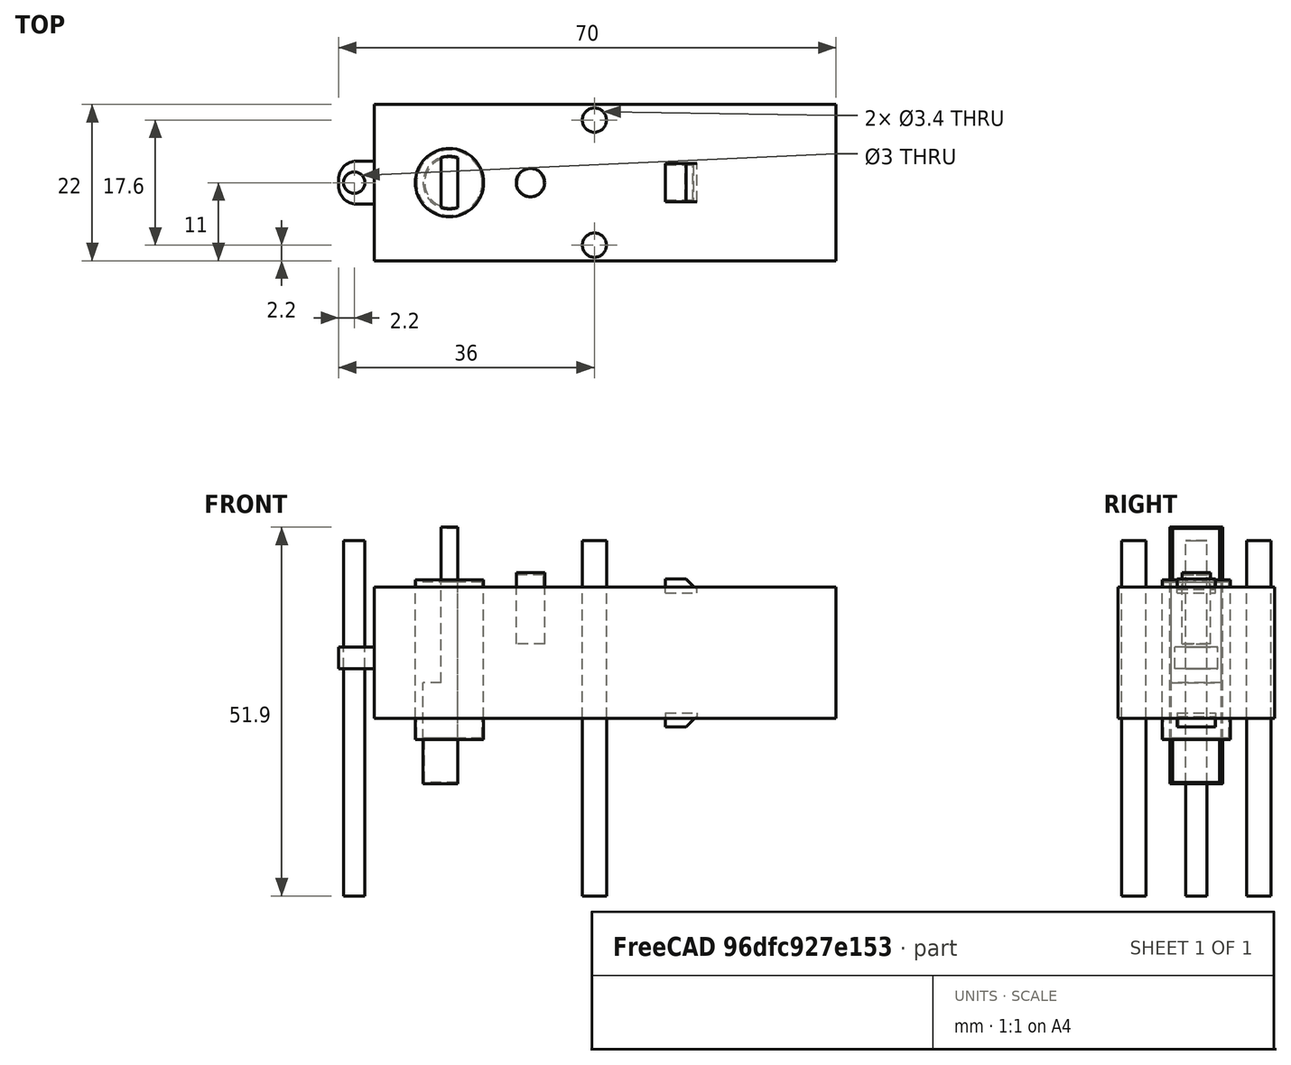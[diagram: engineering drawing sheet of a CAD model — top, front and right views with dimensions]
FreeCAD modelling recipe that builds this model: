
FCSTD DOCUMENT  (FreeCAD 0.16R6703 (Git))
Label: winder
License: All rights reserved
LicenseURL: http://en.wikipedia.org/wiki/All_rights_reserved
objects: Part::Cylinder×12, Part::Box×10, Part::Cut×7, Part::Fuse×7, Part::Chamfer×4, Part::Fillet×2, Part::Mirroring×2, App::DocumentObjectGroup×1
note: 44 computed .brp shape members not serialized (recipe doc carries the construction recipe); baked Part::Feature solids carry a one-line shape summary decoded from their .brp

FEATURE [Part::Box] Box  label="Cube"
  Height = 18.5
  Length = 65
  Placement = pos=(0,-11,0) rot=(0,0,1;0rad)
  Width = 22
FEATURE [Part::Box] Box001  label="Cube001"
  Height = 3
  Length = 10
  Placement = pos=(-5,-3,7) rot=(0,0,1;0rad)
  Width = 6
FEATURE [Part::Cylinder] Cylinder
  Angle = 360
  Height = 10
  Placement = pos=(-2.8,0,3) rot=(0,0,1;0rad)
  Radius = 1.5
FEATURE [Part::Cut] Cut
  Base = -> Box001
  Tool = -> Cylinder
FEATURE [Part::Fillet] Fillet
  Base = -> Cut
  Edges = 1 edges r=2.5: [Edge1]
FEATURE [Part::Fillet] Fillet001
  Base = -> Fillet
  Edges = 1 edges r=2.5: [Edge3]
FEATURE [Part::Cylinder] Cylinder001  label="endhole"
  Angle = 360
  Height = 50
  Placement = pos=(-2.8,0,-25) rot=(0,0,1;0rad)
  Radius = 1.5
FEATURE [Part::Fuse] Fusion
  Base = -> Box
  Tool = -> Fillet001
FEATURE [Part::Cylinder] Cylinder002  label="Cylinder001"
  Angle = 360
  Height = 50
  Placement = pos=(31,8.8,-25) rot=(0,0,1;0rad)
  Radius = 1.7
FEATURE [Part::Cylinder] Cylinder003  label="Cylinder002"
  Angle = 360
  Height = 50
  Placement = pos=(31,-8.8,-25) rot=(0,0,1;0rad)
  Radius = 1.7
FEATURE [Part::Cylinder] Cylinder004  label="body-hole-1"
  Angle = 360
  Height = 50
  Placement = pos=(31,8.8,-25) rot=(0,0,1;0rad)
  Radius = 1.7
FEATURE [Part::Cylinder] Cylinder005  label="body-hole-2"
  Angle = 360
  Height = 50
  Placement = pos=(31,-8.8,-25) rot=(0,0,1;0rad)
  Radius = 1.7
FEATURE [Part::Cut] Cut001
  Base = -> Fusion
  Tool = -> Cylinder002
FEATURE [Part::Cut] Cut002
  Base = -> Cut001
  Tool = -> Cylinder003
FEATURE [Part::Cylinder] Cylinder006  label="Cylinder003"
  Angle = 360
  Height = 10
  Placement = pos=(22,0,10.2) rot=(0,0,1;0rad)
  Radius = 1.85
FEATURE [Part::Cylinder] Cylinder007  label="central-bump"
  Angle = 360
  Height = 10
  Placement = pos=(22,0,10.5) rot=(0,0,1;0rad)
  Radius = 2
FEATURE [Part::Fuse] Fusion001
  Base = -> Cut002
  Tool = -> Cylinder006
FEATURE [Part::Cylinder] Cylinder008  label="Cylinder004"
  Angle = 360
  Height = 22
  Placement = pos=(10.6,0,-2.8) rot=(0,0,1;0rad)
  Radius = 4.6
FEATURE [Part::Cylinder] Cylinder009  label="motor-boss"
  Angle = 360
  Height = 22.5
  Placement = pos=(10.6,0,-3) rot=(0,0,1;0rad)
  Radius = 4.8
FEATURE [Part::Fuse] Fusion002
  Base = -> Fusion001
  Tool = -> Cylinder008
FEATURE [Part::Cylinder] Cylinder010  label="motor-boss001"
  Angle = 360
  Height = 35.7
  Placement = pos=(10.6,0,-9) rot=(0,0,1;0rad)
  Radius = 3.5
FEATURE [Part::Box] Box002  label="Cube002"
  Height = 40
  Length = 10
  Placement = pos=(11.75,-5,-11) rot=(0,0,1;0rad)
  Width = 10
FEATURE [Part::Box] Box003  label="Cube003"
  Height = 40
  Length = 10
  Placement = pos=(-0.55,-5,5) rot=(0,0,1;0rad)
  Width = 10
FEATURE [Part::Cut] Cut003
  Base = -> Cylinder010
  Tool = -> Box002
FEATURE [Part::Cut] Cut004
  Base = -> Cut003
  Tool = -> Box003
FEATURE [Part::Cylinder] Cylinder011  label="motor-boss002"
  Angle = 360
  Height = 36.1
  Placement = pos=(10.6,0,-9.2) rot=(0,0,1;0rad)
  Radius = 3.7
FEATURE [Part::Box] Box004  label="Cube004"
  Height = 40
  Length = 10
  Placement = pos=(11.75,-5,-11) rot=(0,0,1;0rad)
  Width = 10
FEATURE [Part::Box] Box005  label="Cube005"
  Height = 40
  Length = 10
  Placement = pos=(-0.55,-5,5) rot=(0,0,1;0rad)
  Width = 10
FEATURE [Part::Cut] Cut005
  Base = -> Cylinder011
  Tool = -> Box004
FEATURE [Part::Cut] Cut006  label="drive"
  Base = -> Cut005
  Tool = -> Box005
FEATURE [Part::Fuse] Fusion003
  Base = -> Fusion002
  Tool = -> Cut004
FEATURE [Part::Box] Box006  label="Cube006"
  Height = 2
  Length = 4.3
  Placement = pos=(41,-2.5,17.53) rot=(0,0,1;0rad)
  Width = 5
FEATURE [Part::Chamfer] Chamfer
  Base = -> Box006
  Edges = 1 edges r=1.5: [Edge6]
FEATURE [Part::Box] Box007  label="Cube007"
  Height = 2
  Length = 4.3
  Placement = pos=(41,-2.5,17.53) rot=(0,0,1;0rad)
  Width = 5
FEATURE [Part::Chamfer] Chamfer001
  Base = -> Box007
  Edges = 1 edges r=1.5: [Edge6]
FEATURE [Part::Mirroring] Part__Mirroring  label="Chamfer001 (Mirror #1)"
  Base = (0,0,0)
  Normal = (0,0,1)
  Placement = pos=(0,0,18.4) rot=(0,0,1;0rad)
  Source = -> Chamfer001
FEATURE [Part::Fuse] Fusion004
  Base = -> Chamfer
  Tool = -> Part__Mirroring
FEATURE [Part::Box] Box008  label="Cube008"
  Height = 2
  Length = 4.4
  Placement = pos=(41,-2.7,17.63) rot=(0,0,1;0rad)
  Width = 5.4
FEATURE [Part::Chamfer] Chamfer002
  Base = -> Box008
  Edges = 1 edges r=1.5: [Edge6]
FEATURE [Part::Box] Box009  label="Cube009"
  Height = 2
  Length = 4.4
  Placement = pos=(41,-2.7,17.63) rot=(0,0,1;0rad)
  Width = 5.4
FEATURE [Part::Chamfer] Chamfer003
  Base = -> Box009
  Edges = 1 edges r=1.5: [Edge6]
FEATURE [Part::Mirroring] Part__Mirroring001  label="Chamfer001 (Mirror #1)001"
  Base = (0,0,0)
  Normal = (0,0,1)
  Placement = pos=(0,0,18.4) rot=(0,0,1;0rad)
  Source = -> Chamfer003
FEATURE [Part::Fuse] Fusion005  label="hook-bumps"
  Base = -> Chamfer002
  Tool = -> Part__Mirroring001
FEATURE [App::DocumentObjectGroup] Group  label="Motor-holes"
  Group = -> [Cylinder001,Cylinder005,Cylinder004,Cylinder007,Cylinder009,Cut006,Fusion005]
FEATURE [Part::Fuse] Fusion006
  Base = -> Fusion003
  Tool = -> Fusion004
